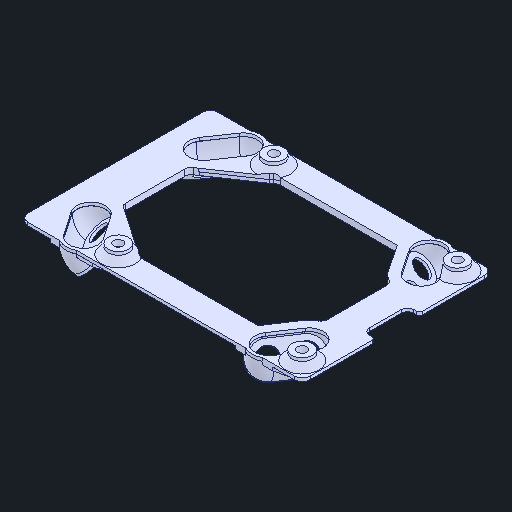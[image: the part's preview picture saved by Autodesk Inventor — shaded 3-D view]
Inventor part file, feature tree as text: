
AUTODESK INVENTOR PART (.ipt)
format: ipt  version: 2023 (Build 270158000, 158)  size: 566,784 bytes
history: native  units: in
note: dims shown in document units (in); Inventor stores cm internally (conversion verified against a paired STEP export)
features: fillet x1
ambient origin geometry x8: Origin, YZ Plane, XZ Plane, XY Plane, X Axis, Y Axis, Z Axis, Center Point
bodies: Solid1 (feature_tree)
feature tree (1):
  fillet  "Fillet4"  [1 undecoded]
note: 1 required parameter value undecoded (feature->parameter linkage not recoverable at this tier; creation-order binding heuristic only, values carry confidence <= 0.55)
